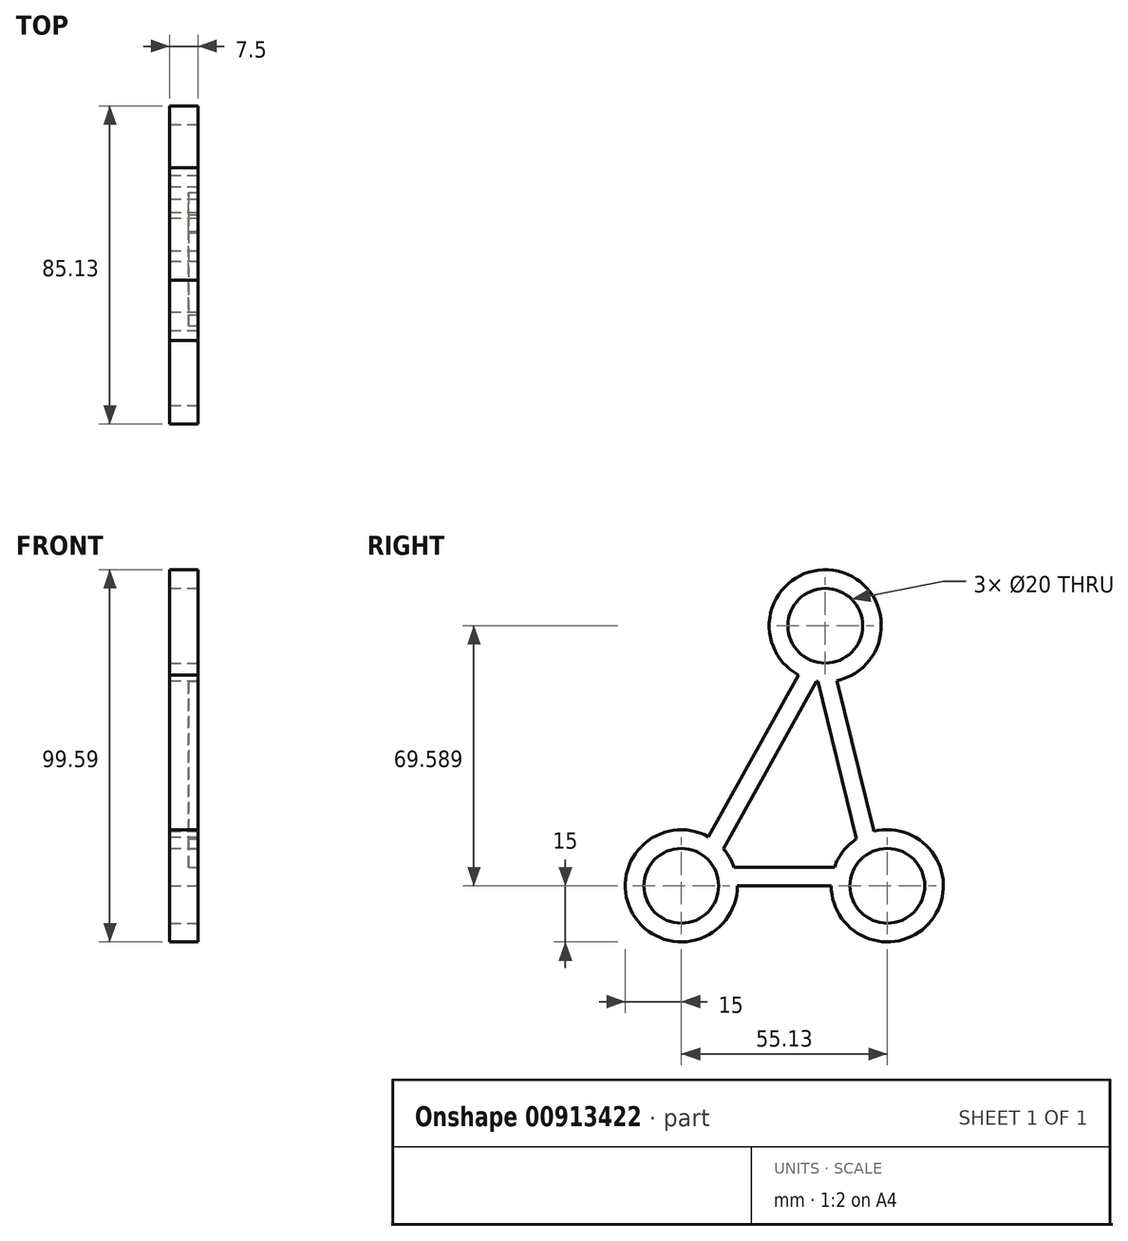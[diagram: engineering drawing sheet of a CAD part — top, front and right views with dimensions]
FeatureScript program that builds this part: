
annotation { "Feature Type Name" : "Feature", "Feature Type Description" : "" }
export const myFeature = defineFeature(function(context is Context, id is Id, definition is map)
    precondition{}
    {
        {
            var Q0;
            Q0=qCreatedBy(makeId("Right.planeOp"),FACE);
            var sketch = newSketch(context, id + "F0", { "sketchPlane" : qUnion([Q0])});
            skLineSegment(sketch, "E0", {"start": v(0.65, 0) * mm, "end": v(55.78, 0) * mm});
            skLineSegment(sketch, "E1", {"start": v(55.78, 0) * mm, "end": v(38.9, 68.84) * mm});
            skLineSegment(sketch, "E2", {"start": v(38.9, 68.84) * mm, "end": v(0.65, 0) * mm});
            skSolve(sketch);
        }
        {
            var Q0;
            Q0 = qSketchRegion(id + "F0", true);
            extrude(context, id + "F1", {"entities" : qUnion([Q0]), "depth" : 7.5 * mm, "offsetDistance" : 25 * mm});
        }
        {
            var Q0;
            Q0=makeQuery(id+"F1.opExtrude","CAP_FACE",FACE,{"disambiguationData":[OSD([sQuery(id+"F0.wireOp",EDGE,"E0"),sQuery(id+"F0.wireOp",EDGE,"E1"),sQuery(id+"F0.wireOp",EDGE,"E2")])],"isStart":false});
            cPlane(context, id + "F2", {"entities" : qUnion([Q0]), "cplaneType" : CPlaneType.OFFSET, "offset" : 0 * mm, "width" : 150 * mm, "height" : 150 * mm});
        }
        {
            var Q0;
            Q0=qCreatedBy(id+"F2.planeOp",FACE);
            var sketch = newSketch(context, id + "F3", { "sketchPlane" : qUnion([Q0])});
            skLineSegment(sketch, "E3.0", {"start": v(37.08, 55.27) * mm, "end": v(49.4, 5) * mm});
            skLineSegment(sketch, "E3.1", {"start": v(9.15, 5) * mm, "end": v(37.08, 55.27) * mm});
            skLineSegment(sketch, "E3.2", {"start": v(49.4, 5) * mm, "end": v(9.15, 5) * mm});
            skSolve(sketch);
        }
        {
            var Q0;
            Q0=makeQuery(id+"F3.imprint","IMPRINT",FACE,{"disambiguationData":[TD([[makeQuery(id+"F3.imprint","IMPRINT",EDGE,{"derivedFrom":sQuery(id+"F3.wireOp",EDGE,"E3.0")}),-1.0]])]});
            extrude(context, id + "F4", {"entities" : qUnion([Q0]), "operationType" : NewBodyOperationType.REMOVE, "oppositeDirection" : true, "depth" : 2.5 * mm, "offsetDistance" : 25 * mm});
        }
        {
            var Q0;
            Q0=qCreatedBy(id+"F2.planeOp",FACE);
            var sketch = newSketch(context, id + "F5", { "sketchPlane" : qUnion([Q0])});
            skCircle(sketch, "E4", {"center": v(39.17, 69.59) * mm, "radius": 15 * mm});
            skCircle(sketch, "E5", {"center": v(55.78, 0) * mm, "radius": 15 * mm});
            skCircle(sketch, "E6", {"center": v(0.65, 0) * mm, "radius": 15 * mm});
            skSolve(sketch);
        }
        {
            var Q0;
            Q0 = qSketchRegion(id + "F5", true);
            extrude(context, id + "F6", {"entities" : qUnion([Q0]), "operationType" : NewBodyOperationType.ADD, "oppositeDirection" : true, "depth" : 7.5 * mm, "offsetDistance" : 25 * mm});
        }
        {
            var Q0;
            Q0=qCreatedBy(id+"F2.planeOp",FACE);
            var sketch = newSketch(context, id + "F7", { "sketchPlane" : qUnion([Q0])});
            skCircle(sketch, "E7", {"center": v(0.65, 0) * mm, "radius": 10 * mm});
            skCircle(sketch, "E8", {"center": v(55.78, 0) * mm, "radius": 10 * mm});
            skCircle(sketch, "E9", {"center": v(39.17, 69.59) * mm, "radius": 10 * mm});
            skSolve(sketch);
        }
        {
            var Q0;
            Q0 = qSketchRegion(id + "F7", true);
            extrude(context, id + "F8", {"entities" : qUnion([Q0]), "operationType" : NewBodyOperationType.REMOVE, "oppositeDirection" : true, "depth" : 25 * mm, "offsetDistance" : 25 * mm});
        }
    });
